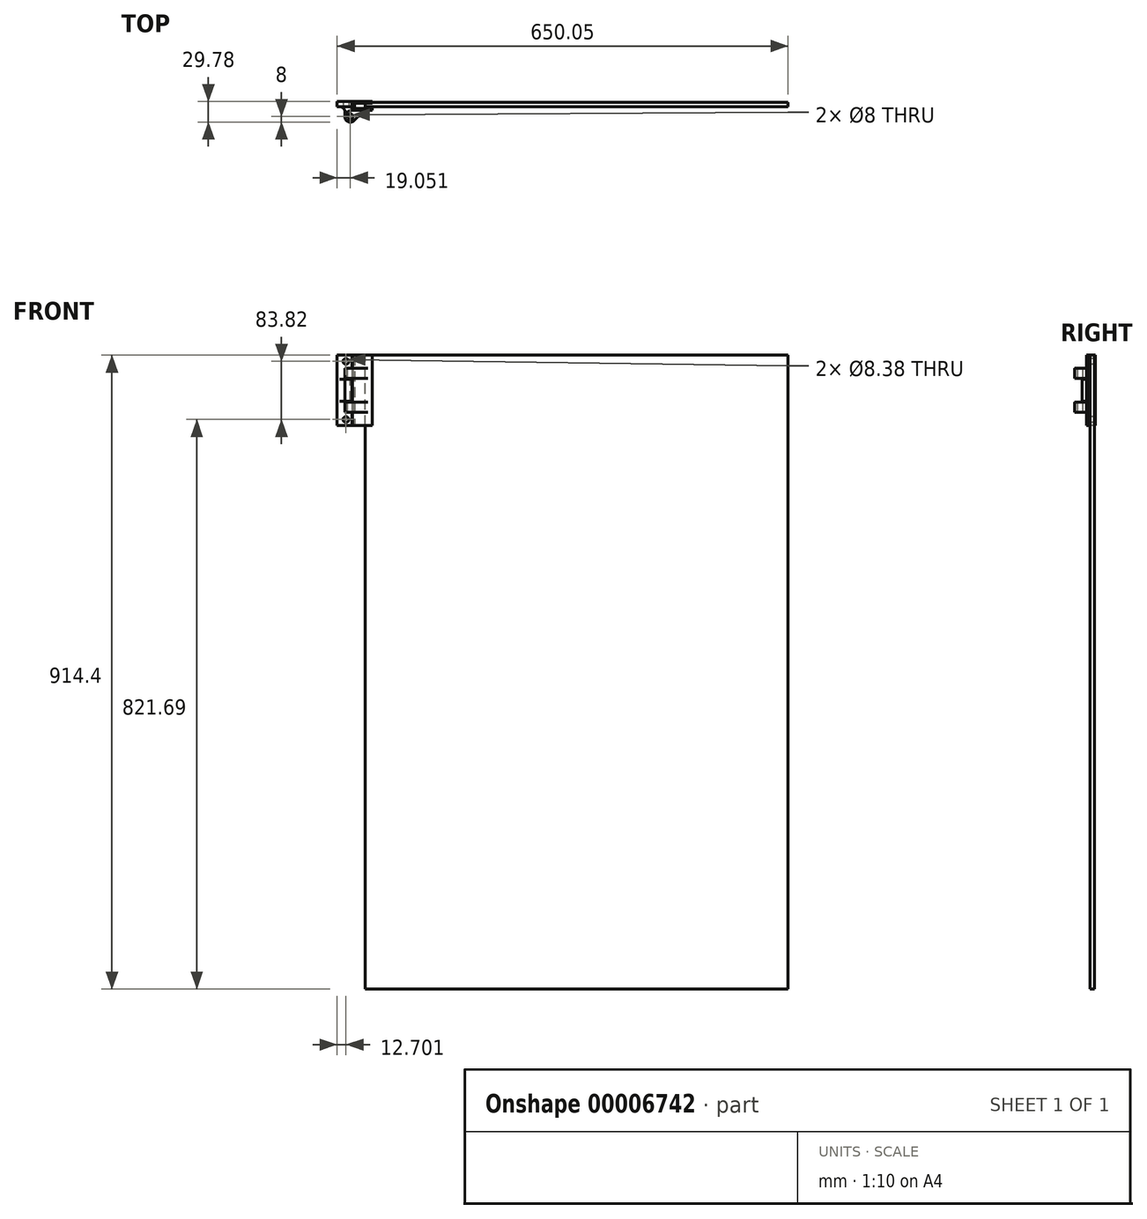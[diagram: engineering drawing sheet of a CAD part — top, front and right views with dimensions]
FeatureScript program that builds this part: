
annotation { "Feature Type Name" : "Feature", "Feature Type Description" : "" }
export const myFeature = defineFeature(function(context is Context, id is Id, definition is map)
    precondition{}
    {
        {
            var Q0;
            Q0=qCreatedBy(makeId("Front.planeOp"),FACE);
            var sketch = newSketch(context, id + "F0", { "sketchPlane" : qUnion([Q0])});
            skLineSegment(sketch, "E0.bottom", {"start": v(0, 0) * mm, "end": v(609.6, 0) * mm});
            skLineSegment(sketch, "E0.top", {"start": v(0, 914.4) * mm, "end": v(609.6, 914.4) * mm});
            skLineSegment(sketch, "E0.left", {"start": v(0, 0) * mm, "end": v(0, 914.4) * mm});
            skLineSegment(sketch, "E0.right", {"start": v(609.6, 0) * mm, "end": v(609.6, 914.4) * mm});
            skSolve(sketch);
        }
        {
            var Q0;
            Q0=makeQuery(id+"F0.imprint","IMPRINT",FACE,{"disambiguationData":[TD([[makeQuery(id+"F0.imprint","IMPRINT",EDGE,{"derivedFrom":sQuery(id+"F0.wireOp",EDGE,"E0.bottom")}),1.0]])]});
            extrude(context, id + "F1", {"entities" : qUnion([Q0]), "oppositeDirection" : true, "depth" : 6.35 * mm, "offsetDistance" : 25.4 * mm});
        }
        {
            var Q0;
            Q0=qCreatedBy(makeId("Front.planeOp"),FACE);
            var sketch = newSketch(context, id + "F2", { "sketchPlane" : qUnion([Q0])});
            skLineSegment(sketch, "E1.bottom", {"start": v(-40.45, 914.4) * mm, "end": v(-19.11, 914.4) * mm});
            skLineSegment(sketch, "E1.top", {"start": v(-40.45, 812.8) * mm, "end": v(-19.11, 812.8) * mm});
            skLineSegment(sketch, "E1.left", {"start": v(-40.45, 914.4) * mm, "end": v(-40.45, 812.8) * mm});
            skLineSegment(sketch, "E1.right", {"start": v(-19.11, 914.4) * mm, "end": v(-19.11, 812.8) * mm});
            skCircle(sketch, "E2", {"center": v(-27.75, 905.5) * mm, "radius": 4.2 * mm});
            skCircle(sketch, "E3", {"center": v(-27.75, 821.69) * mm, "radius": 4.2 * mm});
            skLineSegment(sketch, "E4.bottom", {"start": v(-19.11, 812.8) * mm, "end": v(-1.33, 812.8) * mm});
            skLineSegment(sketch, "E4.top", {"start": v(-19.11, 850.9) * mm, "end": v(-1.33, 850.9) * mm});
            skLineSegment(sketch, "E4.left", {"start": v(-19.11, 812.8) * mm, "end": v(-19.11, 850.9) * mm});
            skLineSegment(sketch, "E4.right", {"start": v(-1.33, 812.8) * mm, "end": v(-1.33, 850.9) * mm});
            skLineSegment(sketch, "E5", {"start": v(-27.75, 905.5) * mm, "end": v(-27.75, 914.4) * mm, "construction": true});
            skLineSegment(sketch, "E6", {"start": v(-27.75, 905.5) * mm, "end": v(-40.45, 905.5) * mm, "construction": true});
            skLineSegment(sketch, "E7", {"start": v(-27.75, 821.69) * mm, "end": v(-27.75, 812.8) * mm, "construction": true});
            skSolve(sketch);
        }
        {
            var Q0;
            Q0=makeQuery(id+"F2.imprint","IMPRINT",FACE,{"disambiguationData":[TD([[makeQuery(id+"F2.imprint","IMPRINT",EDGE,{"derivedFrom":sQuery(id+"F2.wireOp",EDGE,"E1.bottom")}),-1.0]])]});
            extrude(context, id + "F3", {"entities" : qUnion([Q0]), "oppositeDirection" : true, "depth" : 7.62 * mm, "offsetDistance" : 25.4 * mm});
        }
        {
            var Q0;
            Q0=makeQuery(id+"F3.opExtrude","SWEPT_FACE",FACE,{"disambiguationData":[OSD([sQuery(id+"F2.wireOp",EDGE,"E1.bottom")])]});
            var Q1;
            Q1=makeQuery(id+"F3.opExtrude","SWEPT_FACE",FACE,{"disambiguationData":[OSD([sQuery(id+"F2.wireOp",EDGE,"E1.top")])]});
            cPlane(context, id + "F4", {"entities" : qUnion([Q0, Q1]), "cplaneType" : CPlaneType.MID_PLANE, "offset" : 25.4 * mm, "width" : 152.4 * mm, "height" : 152.4 * mm});
        }
        {
            var Q0;
            Q0=qCreatedBy(id+"F4.planeOp",FACE);
            var sketch = newSketch(context, id + "F5", { "sketchPlane" : qUnion([Q0])});
            skCircle(sketch, "E8", {"center": v(-21.4, -14.16) * mm, "radius": 4 * mm});
            skLineSegment(sketch, "E9", {"start": v(-13.78, 0) * mm, "end": v(-13.78, -21.78) * mm});
            skLineSegment(sketch, "E10", {"start": v(-13.78, -21.78) * mm, "end": v(-29.02, -21.78) * mm});
            skLineSegment(sketch, "E11", {"start": v(-29.02, -21.78) * mm, "end": v(-29.02, 0) * mm});
            skLineSegment(sketch, "E12", {"start": v(-29.02, 0) * mm, "end": v(-13.78, 0) * mm});
            skArc(sketch, "E13", {"start": v(-13.78, -7.62) * mm, "mid": v(-16.01, -2.23) * mm, "end": v(-21.4, 0) * mm});
            skLineSegment(sketch, "E14", {"start": v(-25.4, -14.16) * mm, "end": v(-29.02, -14.16) * mm, "construction": true});
            skLineSegment(sketch, "E15", {"start": v(-17.4, -14.16) * mm, "end": v(-13.78, -14.16) * mm, "construction": true});
            skLineSegment(sketch, "E16", {"start": v(-21.4, -18.16) * mm, "end": v(-21.4, -21.78) * mm, "construction": true});
            skLineSegment(sketch, "E17", {"start": v(-21.4, -10.16) * mm, "end": v(-21.4, 0) * mm, "construction": true});
            skLineSegment(sketch, "E18", {"start": v(-21.4, 0) * mm, "end": v(-21.4, 7.62) * mm, "construction": true});
            skLineSegment(sketch, "E19.0", {"start": v(-23.56, 0) * mm, "end": v(-31.94, 0) * mm, "construction": true});
            skPoint(sketch, "E20", {"position": v(-27.75, 0) * mm});
            skArc(sketch, "E21", {"start": v(-21.4, -21.78) * mm, "mid": v(-16.01, -19.55) * mm, "end": v(-13.78, -14.16) * mm});
            skLineSegment(sketch, "E22", {"start": v(-29.02, 0) * mm, "end": v(-36.64, 0) * mm});
            skArc(sketch, "E23", {"start": v(-29.02, -7.62) * mm, "mid": v(-31.25, -2.23) * mm, "end": v(-36.64, 0) * mm});
            skArc(sketch, "E24", {"start": v(-29.02, -14.16) * mm, "mid": v(-26.79, -19.55) * mm, "end": v(-21.4, -21.78) * mm});
            skLineSegment(sketch, "E25", {"start": v(-19.11, 0) * mm, "end": v(-17.2, -1.26) * mm});
            skLineSegment(sketch, "E26", {"start": v(-19.11, 0) * mm, "end": v(-19.11, -2.63) * mm});
            skArc(sketch, "E27", {"start": v(-19.11, -2.63) * mm, "mid": v(-18.42, -5.78) * mm, "end": v(-16.47, -8.35) * mm});
            skArc(sketch, "E28", {"start": v(-13.78, -14.16) * mm, "mid": v(-14.48, -10.96) * mm, "end": v(-16.47, -8.35) * mm});
            skSolve(sketch);
        }
        {
            var Q0;
            Q0=makeQuery(id+"F5.imprint","IMPRINT",FACE,{"disambiguationData":[TD([[makeQuery(id+"F5.imprint","IMPRINT",EDGE,{"derivedFrom":sQuery(id+"F5.wireOp",EDGE,"E8")}),-1.0]])]});
            var Q1;
            {var subQ0=sQuery(id+"F5.wireOp",EDGE,"E13");var subQ1=sQuery(id+"F5.wireOp",EDGE,"E12");var subQ2=makeQuery(id+"F5.imprint","INTERSECT",VERTEX,{"derivedFrom":[subQ1,subQ0]});Q1=makeQuery(id+"F5.imprint","IMPRINT",FACE,{"disambiguationData":[TD([[makeQuery(id+"F5.imprint","IMPRINT",EDGE,{"disambiguationData":[TD([[subQ2,1.0]])],"derivedFrom":subQ0}),1.0]])]});}
            var Q2;
            {var subQ0=sQuery(id+"F5.wireOp",EDGE,"E22");Q2=makeQuery(id+"F5.imprint","IMPRINT",FACE,{"disambiguationData":[TD([[makeQuery(id+"F5.imprint","IMPRINT",EDGE,{"derivedFrom":subQ0}),1.0]])]});}
            extrude(context, id + "F6", {"entities" : qUnion([Q0, Q1, Q2]), "operationType" : NewBodyOperationType.ADD, "endBound" : BoundingType.SYMMETRIC, "oppositeDirection" : true, "depth" : 31.75 * mm, "offsetDistance" : 25.4 * mm});
        }
        {
            var Q0;
            Q0=qCreatedBy(id+"F4.planeOp",FACE);
            var sketch = newSketch(context, id + "F7", { "sketchPlane" : qUnion([Q0])});
            skLineSegment(sketch, "E29.bottom", {"start": v(-18.61, 7.62) * mm, "end": v(10.35, 7.62) * mm});
            skLineSegment(sketch, "E29.top", {"start": v(-18.61, -5.08) * mm, "end": v(10.35, -5.08) * mm});
            skLineSegment(sketch, "E29.left", {"start": v(-18.61, 7.62) * mm, "end": v(-18.61, -5.08) * mm});
            skLineSegment(sketch, "E29.right", {"start": v(10.35, 7.62) * mm, "end": v(10.35, -5.08) * mm});
            skLineSegment(sketch, "E30", {"start": v(-19.11, 10.49) * mm, "end": v(-18.61, 10.49) * mm, "construction": true});
            skLineSegment(sketch, "E31", {"start": v(-18.61, 10.49) * mm, "end": v(-2.35, 10.49) * mm, "construction": true});
            skLineSegment(sketch, "E32", {"start": v(-2.35, 10.49) * mm, "end": v(10.35, 10.49) * mm, "construction": true});
            skLineSegment(sketch, "E33", {"start": v(-19.11, 10.49) * mm, "end": v(-27.75, 10.49) * mm, "construction": true});
            skLineSegment(sketch, "E34.0", {"start": v(-23.56, 0) * mm, "end": v(-31.94, 0) * mm, "construction": true});
            skCircle(sketch, "E35", {"center": v(-21.4, -14.16) * mm, "radius": 4 * mm});
            skCircle(sketch, "E36", {"center": v(-21.4, -14.16) * mm, "radius": 8 * mm});
            skLineSegment(sketch, "E37", {"start": v(-23.54, -6.45) * mm, "end": v(-18.61, -5.08) * mm});
            skArc(sketch, "E38", {"start": v(4.13, -5.08) * mm, "mid": v(-0.61, -6.02) * mm, "end": v(-4.63, -8.7) * mm});
            skLineSegment(sketch, "E39", {"start": v(-4.63, -8.7) * mm, "end": v(-15.74, -19.82) * mm});
            skLineSegment(sketch, "E40.bottom", {"start": v(10.35, 5.08) * mm, "end": v(-15.06, 5.08) * mm});
            skLineSegment(sketch, "E40.top", {"start": v(10.35, -2.54) * mm, "end": v(-15.06, -2.54) * mm});
            skLineSegment(sketch, "E40.left", {"start": v(10.35, 5.08) * mm, "end": v(10.35, -2.54) * mm});
            skLineSegment(sketch, "E40.right", {"start": v(-15.06, 5.08) * mm, "end": v(-15.06, -2.54) * mm});
            skLineSegment(sketch, "E41", {"start": v(-15.06, 5.08) * mm, "end": v(-15.06, 7.62) * mm, "construction": true});
            skLineSegment(sketch, "E42", {"start": v(-15.06, -2.54) * mm, "end": v(-15.06, -5.08) * mm, "construction": true});
            skSolve(sketch);
        }
        {
            var Q0;
            {var subQ7=sQuery(id+"F7.wireOp",EDGE,"E29.bottom");Q0=makeQuery(id+"F7.imprint","IMPRINT",FACE,{"disambiguationData":[TD([[makeQuery(id+"F7.imprint","IMPRINT",EDGE,{"derivedFrom":subQ7}),-1.0]])]});}
            extrude(context, id + "F8", {"entities" : qUnion([Q0]), "endBound" : BoundingType.SYMMETRIC, "depth" : 101.6 * mm, "offsetDistance" : 25.4 * mm});
        }
        {
            var Q0;
            {var subQ1=sQuery(id+"F7.wireOp",EDGE,"E37");Q0=makeQuery(id+"F7.imprint","IMPRINT",FACE,{"disambiguationData":[TD([[makeQuery(id+"F7.imprint","IMPRINT",EDGE,{"derivedFrom":subQ1}),-1.0]])]});}
            var Q1;
            Q1=makeQuery(id+"F7.imprint","IMPRINT",FACE,{"disambiguationData":[TD([[makeQuery(id+"F7.imprint","IMPRINT",EDGE,{"derivedFrom":sQuery(id+"F7.wireOp",EDGE,"E35")}),-1.0]])]});
            extrude(context, id + "F9", {"entities" : qUnion([Q0, Q1]), "operationType" : NewBodyOperationType.ADD, "endBound" : BoundingType.SYMMETRIC, "depth" : 63.5 * mm, "offsetDistance" : 25.4 * mm});
        }
        {
            var Q0;
            Q0=makeQuery(id+"F7.imprint","IMPRINT",FACE,{"disambiguationData":[TD([[makeQuery(id+"F7.imprint","IMPRINT",EDGE,{"derivedFrom":sQuery(id+"F7.wireOp",EDGE,"E35")}),-1.0]])]});
            var Q1;
            {var subQ1=sQuery(id+"F7.wireOp",EDGE,"E37");Q1=makeQuery(id+"F7.imprint","IMPRINT",FACE,{"disambiguationData":[TD([[makeQuery(id+"F7.imprint","IMPRINT",EDGE,{"derivedFrom":subQ1}),-1.0]])]});}
            extrude(context, id + "F10", {"entities" : qUnion([Q0, Q1]), "operationType" : NewBodyOperationType.REMOVE, "endBound" : BoundingType.SYMMETRIC, "depth" : 34.3 * mm, "offsetDistance" : 25.4 * mm});
        }
        {
            var Q0;
            {var subQ0=sQuery(id+"F7.wireOp",EDGE,"E37");var subQ1=sQuery(id+"F7.wireOp",EDGE,"E29.left");var subQ2=sQuery(id+"F7.wireOp",EDGE,"E29.top");Q0=makeQuery(id+"F10.boolean.opBoolean","MERGE",EDGE,{"derivedFrom":[makeQuery(id+"F8.opExtrude","SWEPT_EDGE",EDGE,{"disambiguationData":[OSD([subQ2,subQ1,subQ0])]}),makeQuery(id+"F10.opExtrude","SWEPT_EDGE",EDGE,{"disambiguationData":[OSD([subQ2,subQ1,subQ0])]})]});}
            fillet(context, id + "F11", {"entities" : qUnion([Q0]), "radius" : 2.54 * mm, "tangentPropagation" : true, "allowEdgeOverflow" : false});
        }
    });
